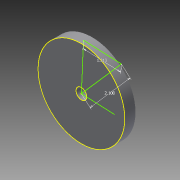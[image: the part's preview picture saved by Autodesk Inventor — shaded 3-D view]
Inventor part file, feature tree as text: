
AUTODESK INVENTOR PART (.ipt)
format: ipt  version: 2013 (Build 170138000, 138)  size: 84,480 bytes
history: native  units: in
note: dims shown in document units (in); Inventor stores cm internally (conversion verified against a paired STEP export)
features: sketch x3, extrude x2
ambient origin geometry x8: Origin, YZ Plane, XZ Plane, XY Plane, X Axis, Y Axis, Z Axis, Center Point
bodies: Solid1 (feature_tree)
feature tree (5):
  extrude  "Extrusion1"  Depth=0.375in TaperAngle=0.0deg
  extrude  "Extrusion2"  Depth=0.375in TaperAngle=0.0deg
  sketch  "Sketch3"  dims[d7=2.1in d8=1.3125in]
  sketch  "Sketch1"  dims[d0=3.0in d1=0.375in d2=0.0in]
  sketch  "Sketch2"  dims[d3=0.375in d4=0.375in d5=0.0in]
